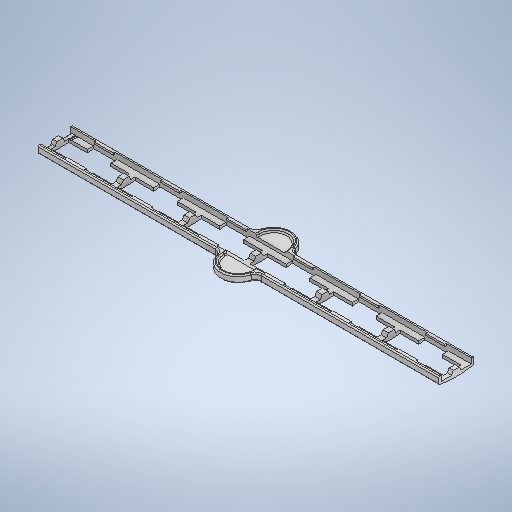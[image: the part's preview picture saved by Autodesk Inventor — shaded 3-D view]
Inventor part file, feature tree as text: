
AUTODESK INVENTOR PART (.ipt)
format: ipt  version: 2025.1 (Build 291241020, 241B)  size: 540,160 bytes
history: native  units: in
note: dims shown in document units (in); Inventor stores cm internally (conversion verified against a paired STEP export)
features: fillet x1
ambient origin geometry x8: Origin, YZ Plane, XZ Plane, XY Plane, X Axis, Y Axis, Z Axis, Center Point
bodies: Solid1 (feature_tree)
feature tree (1):
  fillet  "Fillet43"  [1 undecoded]
note: 1 required parameter value undecoded (feature->parameter linkage not recoverable at this tier; creation-order binding heuristic only, values carry confidence <= 0.55)
